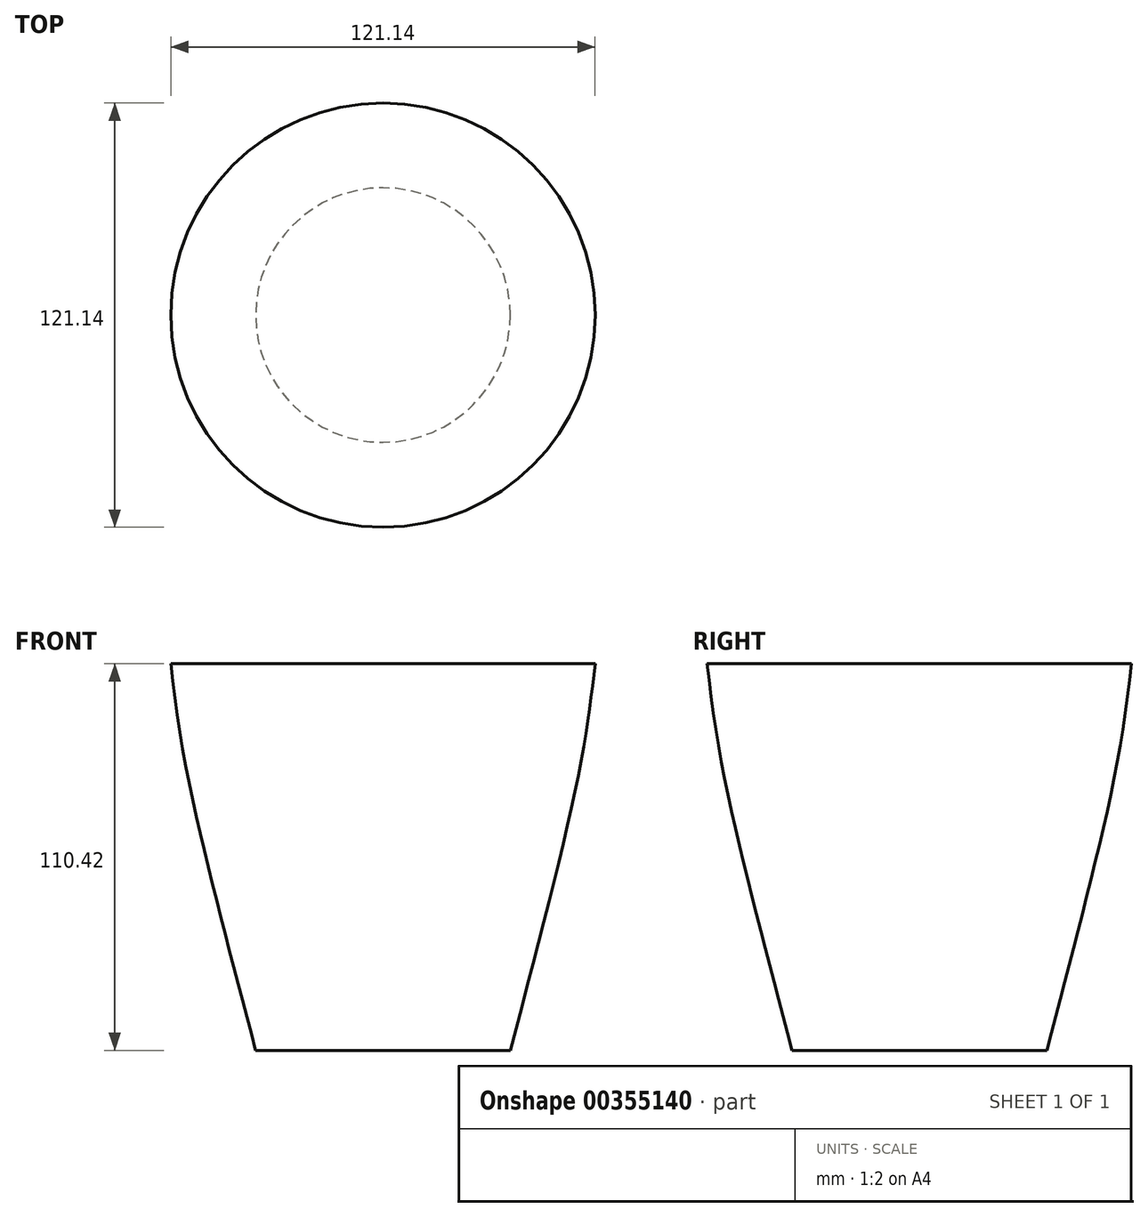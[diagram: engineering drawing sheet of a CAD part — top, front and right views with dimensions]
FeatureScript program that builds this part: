
annotation { "Feature Type Name" : "Feature", "Feature Type Description" : "" }
export const myFeature = defineFeature(function(context is Context, id is Id, definition is map)
    precondition{}
    {
        {
            var Q0;
            Q0=qCreatedBy(makeId("Front.planeOp"),FACE);
            var sketch = newSketch(context, id + "F0", { "sketchPlane" : qUnion([Q0])});
            skLineSegment(sketch, "E0", {"start": v(0, 55.91) * mm, "end": v(60.57, 55.91) * mm});
            skLineSegment(sketch, "E1", {"start": v(0, -54.51) * mm, "end": v(36.34, -54.51) * mm});
            skFitSpline(sketch, "E2", {"points": [v(60.57, 55.91) * mm, v(55.91, 24.7) * mm, v(36.34, -54.51) * mm], "startDerivative": vector(-8.4, -72.38) * mm, "endDerivative": vector(-37.78, -142.98) * mm});
            skLineSegment(sketch, "E3", {"start": v(0, 55.91) * mm, "end": v(0, -54.51) * mm});
            skSolve(sketch);
        }
        {
            var Q0;
            Q0=makeQuery(id+"F0.imprint","IMPRINT",FACE,{"disambiguationData":[TD([[makeQuery(id+"F0.imprint","IMPRINT",EDGE,{"derivedFrom":sQuery(id+"F0.wireOp",EDGE,"E0")}),-1.0]])]});
            var Q1;
            Q1=sQuery(id+"F0.wireOp",EDGE,"E3");
            revolve(context, id + "F1", {"entities" : qUnion([Q0]), "axis" : qUnion([Q1]), "revolveType" : RevolveType.FULL});
        }
    });
